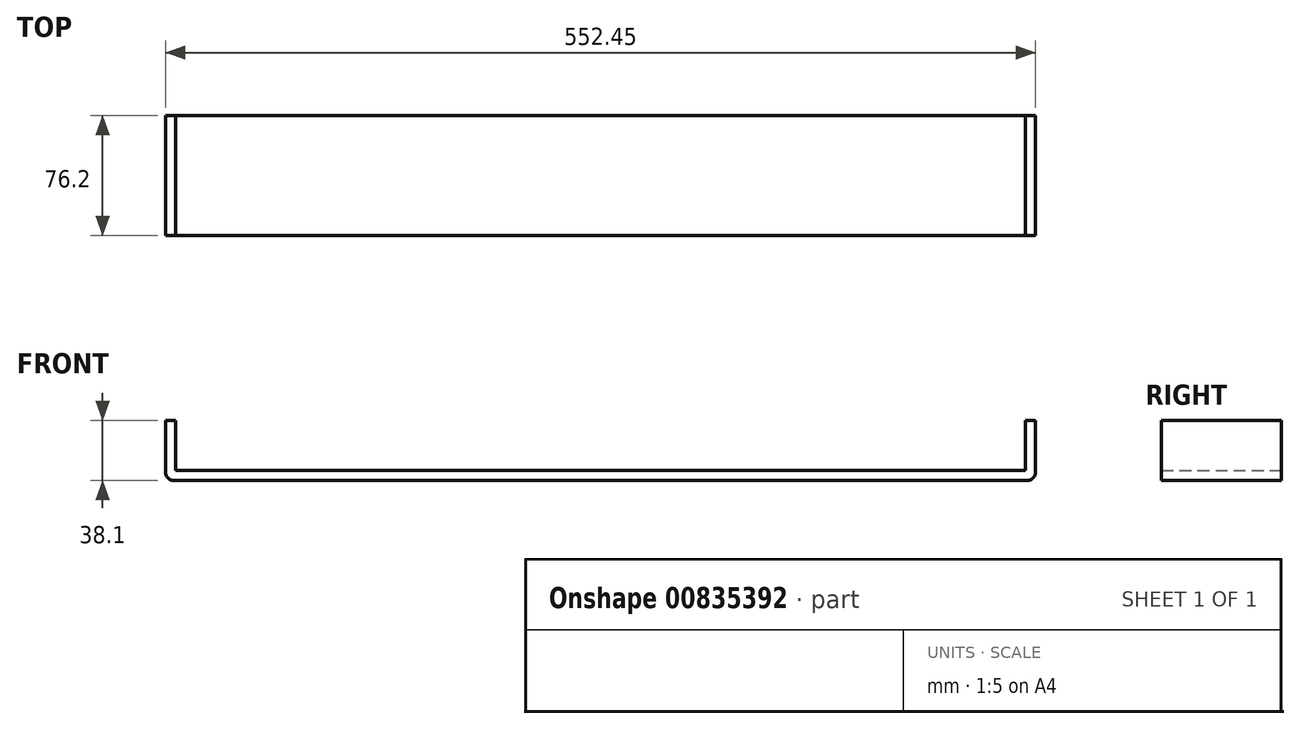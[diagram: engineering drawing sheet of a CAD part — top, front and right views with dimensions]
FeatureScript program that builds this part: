
annotation { "Feature Type Name" : "Feature", "Feature Type Description" : "" }
export const myFeature = defineFeature(function(context is Context, id is Id, definition is map)
    precondition{}
    {
        {
            var Q0;
            Q0=qCreatedBy(makeId("Front.planeOp"),FACE);
            var sketch = newSketch(context, id + "F0", { "sketchPlane" : qUnion([Q0])});
            skLineSegment(sketch, "E0.bottom", {"start": v(0, 0) * mm, "end": v(-552.45, 0) * mm});
            skLineSegment(sketch, "E0.top", {"start": v(0, 38.1) * mm, "end": v(-6.35, 38.1) * mm});
            skLineSegment(sketch, "E0.left", {"start": v(0, 0) * mm, "end": v(0, 38.1) * mm});
            skLineSegment(sketch, "E0.right", {"start": v(-552.45, 0) * mm, "end": v(-552.45, 38.1) * mm});
            skLineSegment(sketch, "E1.bottom", {"start": v(-552.45, 38.1) * mm, "end": v(-546.1, 38.1) * mm});
            skLineSegment(sketch, "E1.left", {"start": v(-552.45, 38.1) * mm, "end": v(-552.45, 6.35) * mm});
            skLineSegment(sketch, "E1.right", {"start": v(-546.1, 38.1) * mm, "end": v(-546.1, 6.35) * mm});
            skLineSegment(sketch, "E2.bottom", {"start": v(-546.1, 6.35) * mm, "end": v(-6.35, 6.35) * mm});
            skLineSegment(sketch, "E2.left", {"start": v(-546.1, 6.35) * mm, "end": v(-546.1, 38.1) * mm});
            skLineSegment(sketch, "E2.right", {"start": v(-6.35, 6.35) * mm, "end": v(-6.35, 38.1) * mm});
            skLineSegment(sketch, "E3.trimOffspring", {"start": v(-546.1, 38.1) * mm, "end": v(-552.45, 38.1) * mm});
            skSolve(sketch);
        }
        {
            var Q0;
            Q0 = qSketchRegion(id + "F0", true);
            extrude(context, id + "F1", {"entities" : qUnion([Q0]), "depth" : 76.2 * mm, "offsetDistance" : 25.4 * mm});
        }
        {
            var Q0;
            Q0=makeQuery(id+"F1.opExtrude","SWEPT_EDGE",EDGE,{"disambiguationData":[OSD([sQuery(id+"F0.wireOp",EDGE,"E0.bottom"),sQuery(id+"F0.wireOp",EDGE,"E0.right")])]});
            fillet(context, id + "F2", {"entities" : qUnion([Q0]), "radius" : 5.08 * mm, "tangentPropagation" : true, "allowEdgeOverflow" : false});
        }
        {
            var Q0;
            Q0=makeQuery(id+"F1.opExtrude","SWEPT_EDGE",EDGE,{"disambiguationData":[OSD([sQuery(id+"F0.wireOp",EDGE,"E0.bottom"),sQuery(id+"F0.wireOp",EDGE,"E0.left")])]});
            fillet(context, id + "F3", {"entities" : qUnion([Q0]), "radius" : 5.08 * mm, "tangentPropagation" : true, "allowEdgeOverflow" : false});
        }
    });
